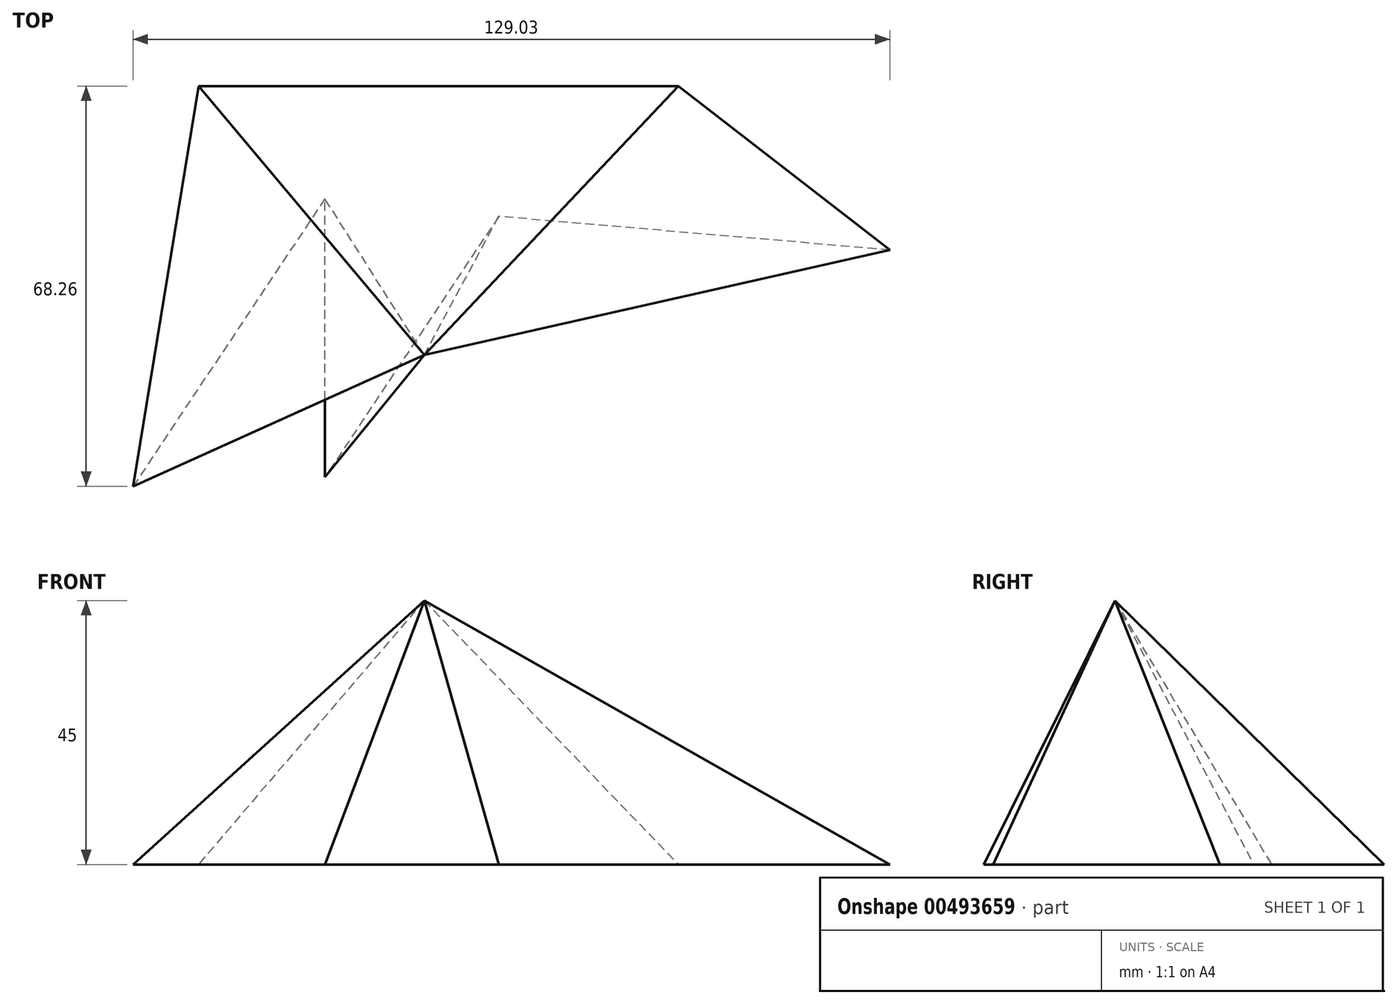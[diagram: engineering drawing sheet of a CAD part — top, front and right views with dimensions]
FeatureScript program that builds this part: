
annotation { "Feature Type Name" : "Feature", "Feature Type Description" : "" }
export const myFeature = defineFeature(function(context is Context, id is Id, definition is map)
    precondition{}
    {
        {
            var Q0;
            Q0=qCreatedBy(makeId("Top.planeOp"),FACE);
            var sketch = newSketch(context, id + "F0", { "sketchPlane" : qUnion([Q0])});
            skLineSegment(sketch, "E0", {"start": v(-38.48, 45.86) * mm, "end": v(43.35, 45.86) * mm});
            skLineSegment(sketch, "E1", {"start": v(43.35, 45.86) * mm, "end": v(79.39, 17.9) * mm});
            skLineSegment(sketch, "E2", {"start": v(79.39, 17.9) * mm, "end": v(12.7, 23.63) * mm});
            skLineSegment(sketch, "E3", {"start": v(12.7, 23.63) * mm, "end": v(-16.93, -20.82) * mm});
            skLineSegment(sketch, "E4", {"start": v(-16.93, -20.82) * mm, "end": v(-16.93, 26.66) * mm});
            skLineSegment(sketch, "E5", {"start": v(-16.93, 26.66) * mm, "end": v(-50.55, -23.77) * mm});
            skLineSegment(sketch, "E6", {"start": v(-49.93, -24.19) * mm, "end": v(-38.48, 45.86) * mm});
            skSolve(sketch);
        }
        {
            var Q0;
            Q0=qCreatedBy(makeId("Top.planeOp"),FACE);
            cPlane(context, id + "F1", {"entities" : qUnion([Q0]), "cplaneType" : CPlaneType.OFFSET, "offset" : 45 * mm, "width" : 150 * mm, "height" : 150 * mm});
        }
        {
            var Q0;
            Q0=qCreatedBy(id+"F1.planeOp",FACE);
            var sketch = newSketch(context, id + "F2", { "sketchPlane" : qUnion([Q0])});
            skPoint(sketch, "E7", {"position": v(0, 0) * mm});
            skSolve(sketch);
        }
        {
            var Q0;
            Q0=sQuery(id+"F2.wireOp",VERTEX,"E7");
            var Q1;
            {var subQ0=sQuery(id+"F0.wireOp",EDGE,"E0");Q1=makeQuery(id+"F0.imprint","IMPRINT",FACE,{"disambiguationData":[TD([[makeQuery(id+"F0.imprint","IMPRINT",EDGE,{"derivedFrom":subQ0}),-1.0]])]});}
            loft(context, id + "F3", {"sheetProfilesArray" : [{ "sheetProfileEntities" : qUnion([Q0]) }, { "sheetProfileEntities" : qUnion([Q1]) }]});
        }
    });
